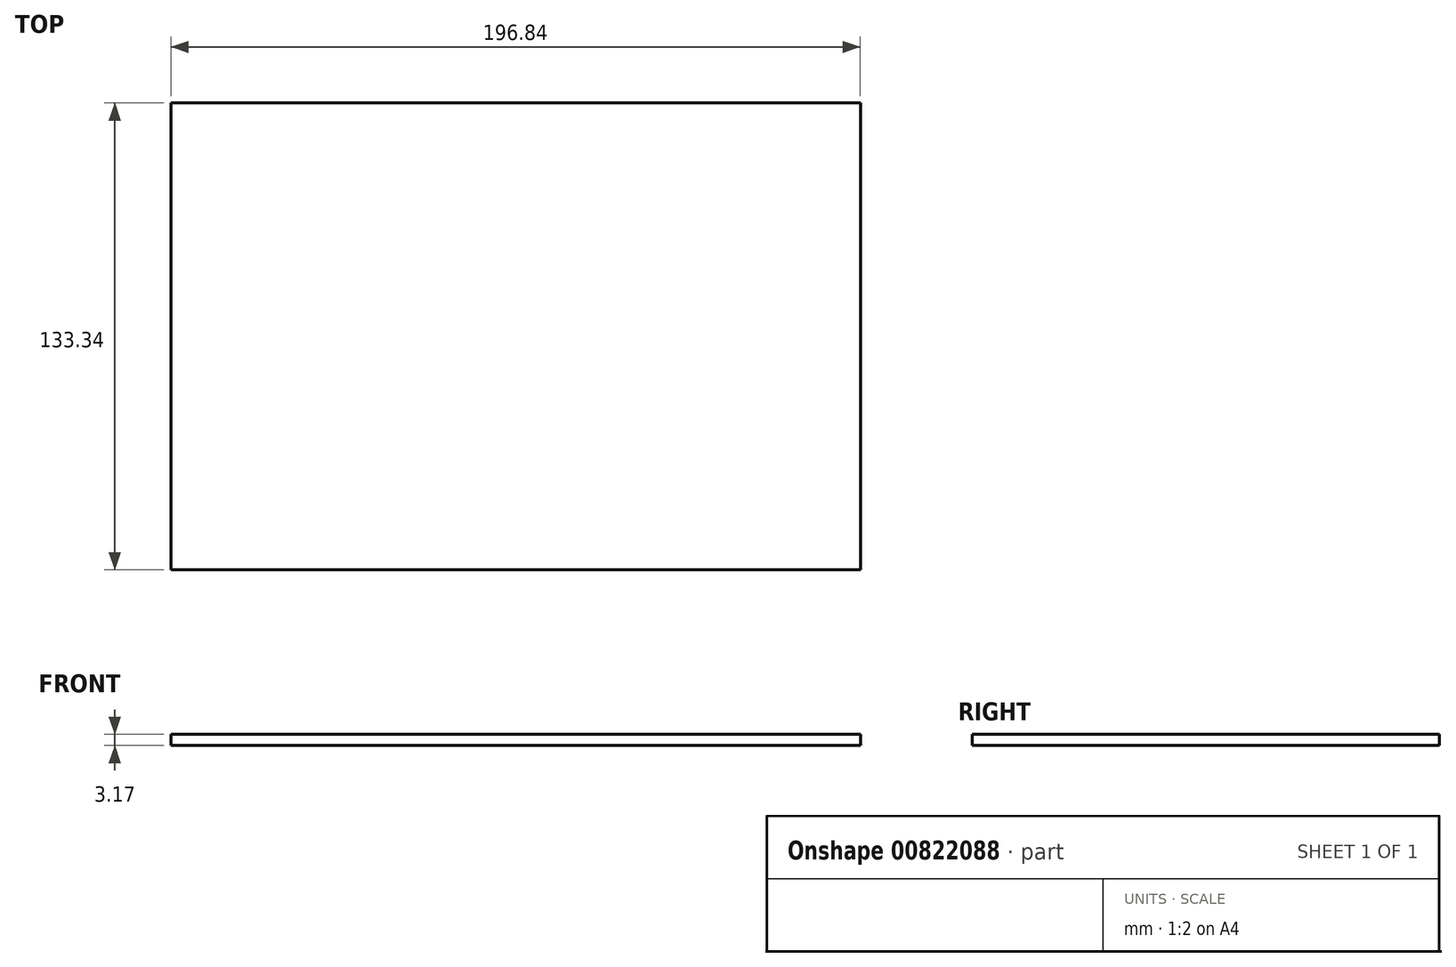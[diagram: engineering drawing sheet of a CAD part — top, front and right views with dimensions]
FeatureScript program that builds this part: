
annotation { "Feature Type Name" : "Feature", "Feature Type Description" : "" }
export const myFeature = defineFeature(function(context is Context, id is Id, definition is map)
    precondition{}
    {
        {
            var Q0;
            Q0=qCreatedBy(makeId("Top.planeOp"),FACE);
            var sketch = newSketch(context, id + "F0", { "sketchPlane" : qUnion([Q0])});
            skLineSegment(sketch, "E0.bottom", {"start": v(98.43, -66.68) * mm, "end": v(-98.42, -66.68) * mm});
            skLineSegment(sketch, "E0.top", {"start": v(98.42, 66.68) * mm, "end": v(-98.43, 66.67) * mm});
            skLineSegment(sketch, "E0.left", {"start": v(98.43, -66.68) * mm, "end": v(98.42, 66.68) * mm});
            skLineSegment(sketch, "E0.right", {"start": v(-98.42, -66.68) * mm, "end": v(-98.43, 66.67) * mm});
            skPoint(sketch, "E0.middle", {"position": v(0, 0) * mm});
            skSolve(sketch);
        }
        {
            var Q0;
            Q0=makeQuery(id+"F0.imprint","IMPRINT",FACE,{"disambiguationData":[TD([[makeQuery(id+"F0.imprint","IMPRINT",EDGE,{"derivedFrom":sQuery(id+"F0.wireOp",EDGE,"E0.bottom")}),-1.0]])]});
            extrude(context, id + "F1", {"entities" : qUnion([Q0]), "depth" : 3.17 * mm, "offsetDistance" : 25.4 * mm});
        }
    });
